# Revit family: Plumbing_Drainage_Menzies-Metal_Clamp-Tite_Box-Scupper_Copper-TPO
name_source: partatom
category: Plumbing Fixtures
revit_build: Autodesk Revit 2018 (Build: 20170223_1515(x64)
units: mm (PartAtom-declared; Revit-internal decimal feet)

## family parameters
Cut with Voids When Loaded = No
Host = Face
OmniClass Number = 23.70.50.21.24.11
OmniClass Title = Roof Waste Water Drains
Part Type = Normal
Room Calculation Point = No
Round Connector Dimension = Use Diameter
Shared = No

## types (2) — shared parameters
Assembly Code = D2040200
Box Length = 1' - 5"
Box Length Note = Cut to suit wall depth.
Default Elevation = 4' - 0"
Description = Clamp-Tite Copper Box Scupper TPO
Drain Flow = 0 GPM
Edition number = 1
Manufacturer = Menzies Metal Products
Pipe Diameter = 3"
Product Guid = 66634ec9-53f4-4fc0-acc2-6e6f6b3c707f
Product Material = Metal - Menzies Metal Products - Copper
Product data url = https://www.bimobject.com
URL = https://www.menzies-metal.com

## per-type parameters (varying)
| type | Model | Weight |
| 3" downspout | 300-3063TPO | 4.40 lbf |
| 3" downspout w/ strainer kit | 300-3063TPO & 300-3199 | 4.50 lbf |

## geometry (parser evidence)
native form markers: Sweep x11
no freeform markers — native parametric forms only
